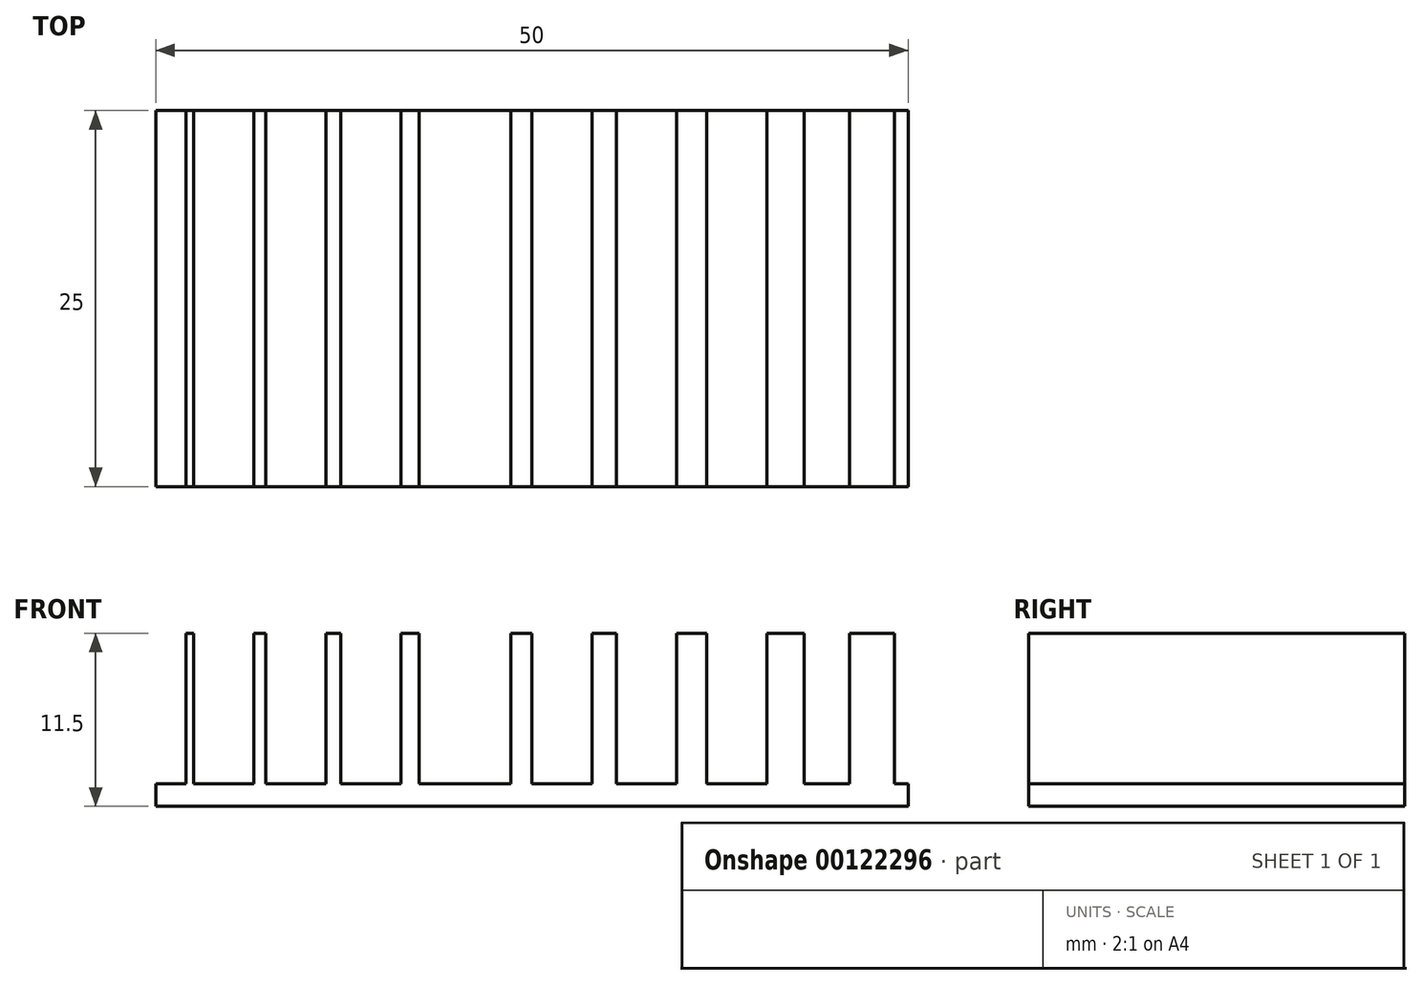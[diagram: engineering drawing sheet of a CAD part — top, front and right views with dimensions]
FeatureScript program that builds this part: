
annotation { "Feature Type Name" : "Feature", "Feature Type Description" : "" }
export const myFeature = defineFeature(function(context is Context, id is Id, definition is map)
    precondition{}
    {
        {
            var Q0;
            Q0=qCreatedBy(makeId("Front.planeOp"),FACE);
            var sketch = newSketch(context, id + "F0", { "sketchPlane" : qUnion([Q0])});
            skLineSegment(sketch, "E0", {"start": v(0, 0) * mm, "end": v(50, 0) * mm});
            skLineSegment(sketch, "E1", {"start": v(0, 0) * mm, "end": v(0, 1.5) * mm});
            skLineSegment(sketch, "E2", {"start": v(0, 1.5) * mm, "end": v(50, 1.5) * mm});
            skLineSegment(sketch, "E3", {"start": v(50, 0) * mm, "end": v(50, 1.5) * mm});
            skSolve(sketch);
        }
        {
            var Q0;
            Q0=makeQuery(id+"F0.imprint","IMPRINT",FACE,{"disambiguationData":[TD([[makeQuery(id+"F0.imprint","IMPRINT",EDGE,{"derivedFrom":sQuery(id+"F0.wireOp",EDGE,"E0")}),1.0]])]});
            extrude(context, id + "F1", {"entities" : qUnion([Q0]), "oppositeDirection" : true, "depth" : 25 * mm});
        }
        {
            var Q0;
            Q0=makeQuery(id+"F1.opExtrude","SWEPT_FACE",FACE,{"disambiguationData":[OSD([sQuery(id+"F0.wireOp",EDGE,"E2")])]});
            cPlane(context, id + "F2", {"entities" : qUnion([Q0]), "cplaneType" : CPlaneType.OFFSET, "offset" : 0 * mm, "width" : 150 * mm, "height" : 150 * mm});
        }
        {
            var Q0;
            Q0=qCreatedBy(id+"F2.planeOp",FACE);
            var sketch = newSketch(context, id + "F3", { "sketchPlane" : qUnion([Q0])});
            skLineSegment(sketch, "E4.0", {"start": v(0, 0) * mm, "end": v(50, 0) * mm, "construction": true});
            skLineSegment(sketch, "E4.1", {"start": v(0, 25) * mm, "end": v(50, 25) * mm, "construction": true});
            skLineSegment(sketch, "E5", {"start": v(2, 25) * mm, "end": v(2, 0) * mm});
            skLineSegment(sketch, "E6", {"start": v(2, 0) * mm, "end": v(2.5, 0) * mm});
            skLineSegment(sketch, "E7", {"start": v(2.5, 0) * mm, "end": v(2.5, 25) * mm});
            skLineSegment(sketch, "E8", {"start": v(2.5, 25) * mm, "end": v(2, 25) * mm});
            skLineSegment(sketch, "E9", {"start": v(6.5, 25) * mm, "end": v(6.5, 0) * mm});
            skLineSegment(sketch, "E10", {"start": v(6.5, 0) * mm, "end": v(7.3, 0) * mm});
            skLineSegment(sketch, "E11", {"start": v(7.3, 0) * mm, "end": v(7.3, 25) * mm});
            skLineSegment(sketch, "E12", {"start": v(7.3, 25) * mm, "end": v(6.5, 25) * mm});
            skLineSegment(sketch, "E13", {"start": v(11.3, 0) * mm, "end": v(11.3, 25) * mm});
            skLineSegment(sketch, "E14", {"start": v(11.3, 25) * mm, "end": v(12.3, 25) * mm});
            skLineSegment(sketch, "E15", {"start": v(12.3, 25) * mm, "end": v(12.3, 0) * mm});
            skLineSegment(sketch, "E16", {"start": v(12.3, 0) * mm, "end": v(11.3, 0) * mm});
            skLineSegment(sketch, "E17", {"start": v(23.6, 0) * mm, "end": v(23.6, 25) * mm});
            skLineSegment(sketch, "E18", {"start": v(23.6, 25) * mm, "end": v(25, 25) * mm});
            skLineSegment(sketch, "E19", {"start": v(25, 25) * mm, "end": v(25, 0) * mm});
            skLineSegment(sketch, "E20", {"start": v(25, 0) * mm, "end": v(23.6, 0) * mm});
            skLineSegment(sketch, "E21", {"start": v(16.3, 0) * mm, "end": v(16.3, 25) * mm});
            skLineSegment(sketch, "E22", {"start": v(16.3, 25) * mm, "end": v(17.5, 25) * mm});
            skLineSegment(sketch, "E23", {"start": v(17.5, 25) * mm, "end": v(17.5, 0) * mm});
            skLineSegment(sketch, "E24", {"start": v(17.5, 0) * mm, "end": v(16.3, 0) * mm});
            skLineSegment(sketch, "E25", {"start": v(29, 0) * mm, "end": v(29, 25) * mm});
            skLineSegment(sketch, "E26", {"start": v(29, 25) * mm, "end": v(30.6, 25) * mm});
            skLineSegment(sketch, "E27", {"start": v(30.6, 25) * mm, "end": v(30.6, 0) * mm});
            skLineSegment(sketch, "E28", {"start": v(30.6, 0) * mm, "end": v(29, 0) * mm});
            skLineSegment(sketch, "E29", {"start": v(34.6, 0) * mm, "end": v(34.6, 25) * mm});
            skLineSegment(sketch, "E30", {"start": v(34.6, 25) * mm, "end": v(36.6, 25) * mm});
            skLineSegment(sketch, "E31", {"start": v(36.6, 25) * mm, "end": v(36.6, 0) * mm});
            skLineSegment(sketch, "E32", {"start": v(36.6, 0) * mm, "end": v(34.6, 0) * mm});
            skLineSegment(sketch, "E33", {"start": v(40.6, 0) * mm, "end": v(40.6, 25) * mm});
            skLineSegment(sketch, "E34", {"start": v(40.6, 25) * mm, "end": v(43.1, 25) * mm});
            skLineSegment(sketch, "E35", {"start": v(43.1, 25) * mm, "end": v(43.1, 0) * mm});
            skLineSegment(sketch, "E36", {"start": v(43.1, 0) * mm, "end": v(40.6, 0) * mm});
            skLineSegment(sketch, "E37", {"start": v(46.1, 0) * mm, "end": v(46.1, 25) * mm});
            skLineSegment(sketch, "E38", {"start": v(46.1, 25) * mm, "end": v(49.1, 25) * mm});
            skLineSegment(sketch, "E39", {"start": v(49.1, 25) * mm, "end": v(49.1, 0) * mm});
            skLineSegment(sketch, "E40", {"start": v(49.1, 0) * mm, "end": v(46.1, 0) * mm});
            skSolve(sketch);
        }
        {
            var Q0;
            Q0 = qSketchRegion(id + "F3", true);
            extrude(context, id + "F4", {"entities" : qUnion([Q0]), "operationType" : NewBodyOperationType.ADD, "depth" : 10 * mm});
        }
    });
